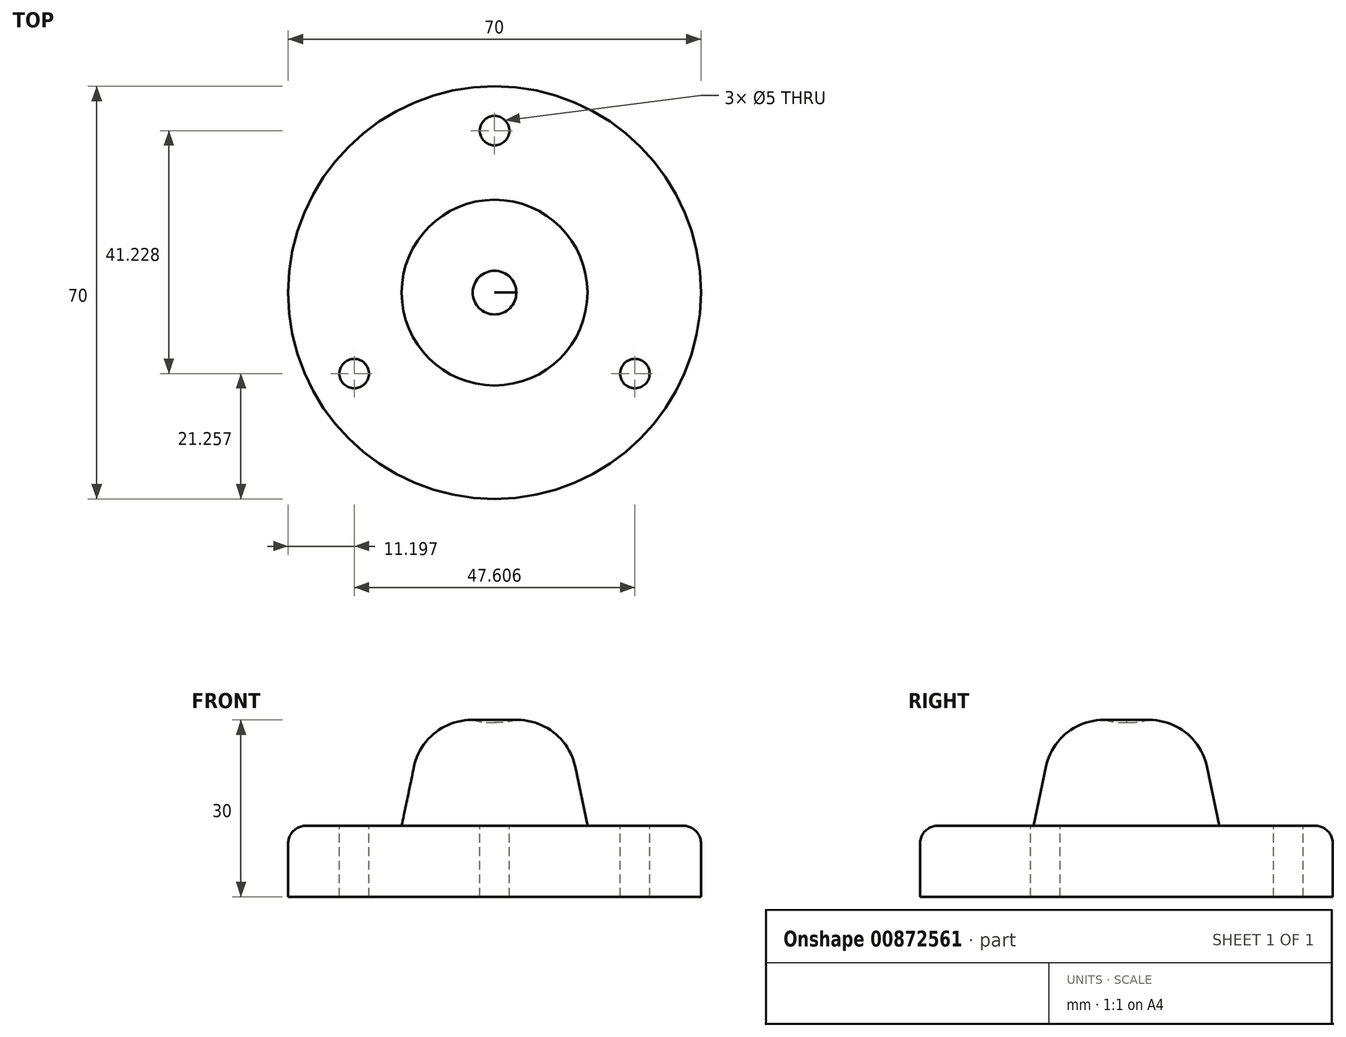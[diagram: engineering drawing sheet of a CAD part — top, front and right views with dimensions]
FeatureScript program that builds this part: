
annotation { "Feature Type Name" : "Feature", "Feature Type Description" : "" }
export const myFeature = defineFeature(function(context is Context, id is Id, definition is map)
    precondition{}
    {
        {
            var Q0;
            Q0=qCreatedBy(makeId("Front.planeOp"),FACE);
            var sketch = newSketch(context, id + "F0", { "sketchPlane" : qUnion([Q0])});
            skLineSegment(sketch, "E0", {"start": v(0, 0) * mm, "end": v(0, 29.56) * mm});
            skLineSegment(sketch, "E1", {"start": v(3.7, 30) * mm, "end": v(3.88, 30) * mm});
            skLineSegment(sketch, "E2", {"start": v(13.66, 22.05) * mm, "end": v(15.75, 12.05) * mm});
            skLineSegment(sketch, "E3", {"start": v(15.75, 12.05) * mm, "end": v(32, 12.05) * mm});
            skLineSegment(sketch, "E4", {"start": v(35, 9.05) * mm, "end": v(35, 0) * mm});
            skLineSegment(sketch, "E5", {"start": v(35, 0) * mm, "end": v(0, 0) * mm});
            skPoint(sketch, "E6.visualSharp", {"position": v(12, 30) * mm});
            skArc(sketch, "E6.filletArc", {"start": v(13.66, 22.05) * mm, "mid": v(10.18, 27.76) * mm, "end": v(3.88, 30) * mm});
            skPoint(sketch, "E7.visualSharp", {"position": v(35, 12.05) * mm});
            skArc(sketch, "E7.filletArc", {"start": v(35, 9.05) * mm, "mid": v(34.12, 11.17) * mm, "end": v(32, 12.05) * mm});
            skPoint(sketch, "E8.orphan", {"position": v(0, 30) * mm});
            skFitSpline(sketch, "E9", {"points": [v(3.7, 30) * mm, v(0, 29.56) * mm], "startDerivative": vector(-2.49, 0.03) * mm, "endDerivative": vector(-10.07, 0.11) * mm});
            skSolve(sketch);
        }
        {
            var Q0;
            Q0=makeQuery(id+"F0.imprint","IMPRINT",FACE,{"disambiguationData":[TD([[makeQuery(id+"F0.imprint","IMPRINT",EDGE,{"derivedFrom":sQuery(id+"F0.wireOp",EDGE,"E0")}),-1.0]])]});
            var Q1;
            Q1=sQuery(id+"F0.wireOp",EDGE,"E0");
            revolve(context, id + "F1", {"surfaceOperationType" : NewSurfaceOperationType.NEW, "entities" : qUnion([Q0]), "axis" : qUnion([Q1]), "revolveType" : RevolveType.FULL});
        }
        {
            var Q0;
            Q0=makeQuery(id+"F1.opRevolve","SWEPT_FACE",FACE,{"disambiguationData":[OSD([sQuery(id+"F0.wireOp",EDGE,"E3")])]});
            var sketch = newSketch(context, id + "F2", { "sketchPlane" : qUnion([Q0])});
            skLineSegment(sketch, "E10", {"start": v(0, 0) * mm, "end": v(0, 32) * mm, "construction": true});
            skLineSegment(sketch, "E11.1.0", {"start": v(-4.33, -7.5) * mm, "end": v(-32.04, -23.5) * mm, "construction": true});
            skLineSegment(sketch, "E11.2.0", {"start": v(4.33, -7.5) * mm, "end": v(32.04, -23.5) * mm, "construction": true});
            skPoint(sketch, "E11.center", {"position": v(0, -5) * mm});
            skCircle(sketch, "E12", {"center": v(0, 27.49) * mm, "radius": 2.5 * mm});
            skCircle(sketch, "E13.1.0", {"center": v(-23.8, -13.74) * mm, "radius": 2.5 * mm});
            skCircle(sketch, "E13.2.0", {"center": v(23.8, -13.74) * mm, "radius": 2.5 * mm});
            skPoint(sketch, "E13.center", {"position": v(0, 0) * mm});
            skSolve(sketch);
        }
        {
            var Q0;
            Q0=makeQuery(id+"F2.imprint","IMPRINT",FACE,{"disambiguationData":[TD([[makeQuery(id+"F2.imprint","IMPRINT",EDGE,{"derivedFrom":sQuery(id+"F2.wireOp",EDGE,"E12")}),1.0]])]});
            var Q1;
            Q1=makeQuery(id+"F2.imprint","IMPRINT",FACE,{"disambiguationData":[TD([[makeQuery(id+"F2.imprint","IMPRINT",EDGE,{"derivedFrom":sQuery(id+"F2.wireOp",EDGE,"E13.2.0")}),1.0]])]});
            var Q2;
            Q2=makeQuery(id+"F2.imprint","IMPRINT",FACE,{"disambiguationData":[TD([[makeQuery(id+"F2.imprint","IMPRINT",EDGE,{"derivedFrom":sQuery(id+"F2.wireOp",EDGE,"E13.1.0")}),1.0]])]});
            var Q3;
            Q3=sQuery(id+"F2.wireOp",EDGE,"E12");
            var Q4;
            Q4=sQuery(id+"F2.wireOp",EDGE,"E13.2.0");
            var Q5;
            Q5=sQuery(id+"F2.wireOp",EDGE,"E13.1.0");
            extrude(context, id + "F3", {"entities" : qUnion([Q0, Q1, Q2]), "operationType" : NewBodyOperationType.REMOVE, "surfaceEntities" : qUnion([Q3, Q4, Q5]), "oppositeDirection" : true, "depth" : 25 * mm, "offsetDistance" : 25 * mm});
        }
        {
            var Q0;
            Q0=makeQuery(id+"F1.opRevolve","SWEPT_FACE",FACE,{"disambiguationData":[OSD([sQuery(id+"F0.wireOp",EDGE,"E5")])]});
            var sketch = newSketch(context, id + "F4", { "sketchPlane" : qUnion([Q0])});
            skCircle(sketch, "E14", {"center": v(0, 0) * mm, "radius": 5 * mm});
            skSolve(sketch);
        }
        {
            var Q0;
            Q0 = qSketchRegion(id + "F4", true);
            extrude(context, id + "F5", {"entities" : qUnion([Q0]), "operationType" : NewBodyOperationType.ADD, "oppositeDirection" : true, "depth" : 29 * mm, "offsetDistance" : 25 * mm});
        }
    });
